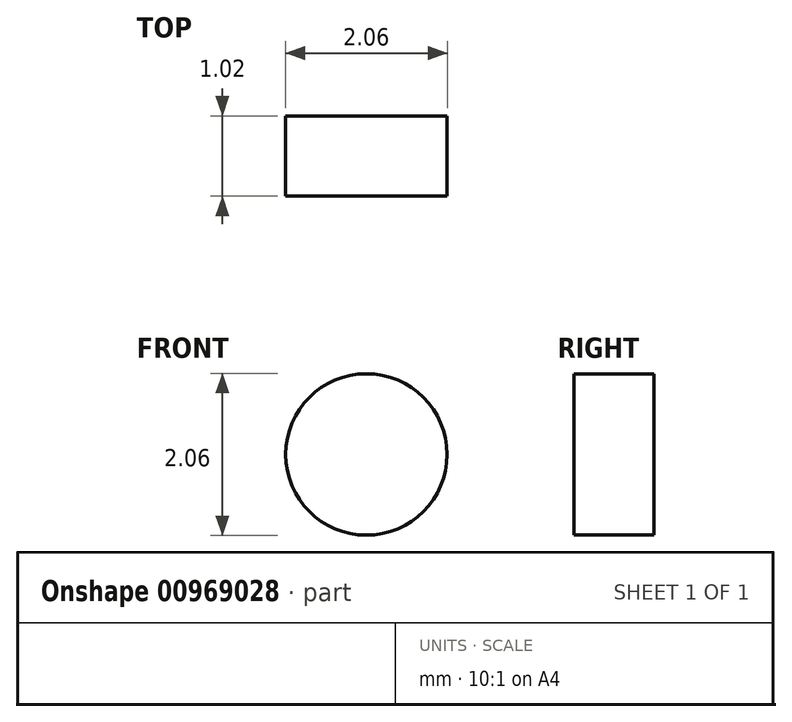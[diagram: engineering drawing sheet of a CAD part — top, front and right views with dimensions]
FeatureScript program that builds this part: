
annotation { "Feature Type Name" : "Feature", "Feature Type Description" : "" }
export const myFeature = defineFeature(function(context is Context, id is Id, definition is map)
    precondition{}
    {
        {
            var Q0;
            Q0=qCreatedBy(makeId("Front.planeOp"),FACE);
            var sketch = newSketch(context, id + "F0", { "sketchPlane" : qUnion([Q0])});
            skCircle(sketch, "E0", {"center": v(0, 0) * mm, "radius": 1.03 * mm});
            skSolve(sketch);
        }
        {
            var Q0;
            Q0=makeQuery(id+"F0.imprint","IMPRINT",FACE,{"disambiguationData":[TD([[makeQuery(id+"F0.imprint","IMPRINT",EDGE,{"derivedFrom":sQuery(id+"F0.wireOp",EDGE,"E0")}),1.0]])]});
            extrude(context, id + "F1", {"entities" : qUnion([Q0]), "depth" : 1.02 * mm, "offsetDistance" : 25.4 * mm});
        }
    });
